# Revit family: Grab_Bar-Bobrick-Fino-B-9807_Series
name_source: partatom
category: Specialty Equipment
revit_build: Autodesk Revit 2018 (Build: 20170223_1515(x64)
units: mm (PartAtom-declared; Revit-internal decimal feet)

## family parameters
Cut with Voids When Loaded = No
Host = Face
OmniClass Number = 23.40.20.21
OmniClass Title = Toilet and Bath Specialties
Part Type = Normal
Room Calculation Point = No
Round Connector Dimension = Use Diameter
Shared = Yes

## types (4) — shared parameters
ADA Compliant = Yes
Assembly Code = C1030200
Default Elevation = 0"
Description = Fino Collection 1½" (38mm) diameter stainless steel grab bars with concealed flange
Finish = Stainless_Steel-Bobrick-Type_303-Satin_Finish
Flange Cover Diameter = 2"
Flange Cover Radius = 1"
Flange Cover Thickness Total = 1/2"
Grab Bar Diameter = 1 1/2"
Installation Type = Wall Mounted
Load Capacity = 1,322lbs (600kgs)
Manufacturer = Bobrick
Material = Stainless_Steel-Bobrick-Type_303-Satin_Finish
Mounting Height From Floor = 29 1/2"
Price = Prices may vary. Please consult Manufacturer Representative for most up-to-date price list.
URL = https://www.bobrick.com
Wall And Grab Bar Clearance = 2 1/4"

## per-type parameters (varying)
| type | Model |
| B-9807-18" | B-9807-18 |
| B-9807-24" | B-9807-24 |
| B-9807-36" | B-9807-36 |
| B-9807-42" | B-9807-42 |

## geometry (parser evidence)
native form markers: Sweep x3
no freeform markers — native parametric forms only
